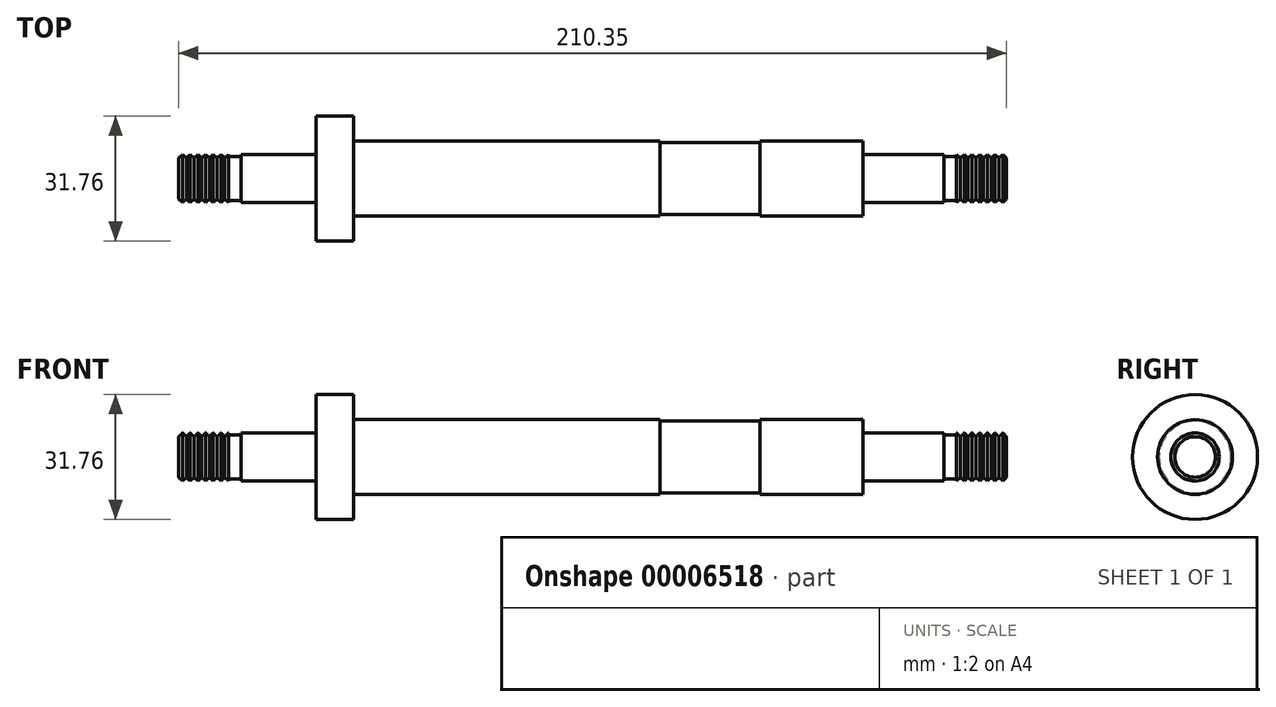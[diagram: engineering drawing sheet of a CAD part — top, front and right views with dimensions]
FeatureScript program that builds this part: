
annotation { "Feature Type Name" : "Feature", "Feature Type Description" : "" }
export const myFeature = defineFeature(function(context is Context, id is Id, definition is map)
    precondition{}
    {
        {
            var Q0;
            Q0=qCreatedBy(makeId("Top.planeOp"),FACE);
            var sketch = newSketch(context, id + "F0", { "sketchPlane" : qUnion([Q0])});
            skLineSegment(sketch, "E0", {"start": v(-288.9, 0) * mm, "end": v(293.4, 0) * mm});
            skLineSegment(sketch, "E1", {"start": v(-256.54, 0) * mm, "end": v(-256.54, 6.14) * mm});
            skLineSegment(sketch, "E2", {"start": v(-256.54, 6.14) * mm, "end": v(-243.84, 6.14) * mm});
            skLineSegment(sketch, "E3", {"start": v(-243.84, 6.14) * mm, "end": v(-243.84, 5.59) * mm});
            skLineSegment(sketch, "E4", {"start": v(-243.84, 5.59) * mm, "end": v(-240.66, 5.59) * mm});
            skLineSegment(sketch, "E5", {"start": v(-240.66, 5.59) * mm, "end": v(-240.66, 6.14) * mm});
            skLineSegment(sketch, "E6", {"start": v(-240.66, 6.14) * mm, "end": v(-221.61, 6.14) * mm});
            skLineSegment(sketch, "E7", {"start": v(-221.61, 6.14) * mm, "end": v(-221.61, 15.88) * mm});
            skLineSegment(sketch, "E8", {"start": v(-221.61, 15.88) * mm, "end": v(-212.09, 15.88) * mm});
            skLineSegment(sketch, "E9", {"start": v(-212.09, 15.88) * mm, "end": v(-212.09, 9.51) * mm});
            skLineSegment(sketch, "E10", {"start": v(-212.09, 9.51) * mm, "end": v(-134.3, 9.51) * mm});
            skLineSegment(sketch, "E11", {"start": v(-134.3, 9.51) * mm, "end": v(-134.3, 9.13) * mm});
            skLineSegment(sketch, "E12", {"start": v(-134.3, 9.13) * mm, "end": v(-108.9, 9.13) * mm});
            skLineSegment(sketch, "E13", {"start": v(-108.9, 9.13) * mm, "end": v(-108.9, 9.51) * mm});
            skLineSegment(sketch, "E14", {"start": v(-108.9, 9.51) * mm, "end": v(-82.7, 9.51) * mm});
            skLineSegment(sketch, "E15", {"start": v(-82.7, 9.51) * mm, "end": v(-82.7, 6.14) * mm});
            skLineSegment(sketch, "E16", {"start": v(-82.7, 6.14) * mm, "end": v(-62.07, 6.14) * mm});
            skLineSegment(sketch, "E17", {"start": v(-62.07, 6.14) * mm, "end": v(-62.07, 5.59) * mm});
            skLineSegment(sketch, "E18", {"start": v(-62.07, 5.59) * mm, "end": v(-58.9, 5.59) * mm});
            skLineSegment(sketch, "E19", {"start": v(-58.9, 5.59) * mm, "end": v(-58.9, 6.14) * mm});
            skLineSegment(sketch, "E20", {"start": v(-58.9, 6.14) * mm, "end": v(-46.2, 6.14) * mm});
            skLineSegment(sketch, "E21", {"start": v(-46.2, 6.14) * mm, "end": v(-46.2, 0) * mm});
            skPoint(sketch, "E22", {"position": v(-256.54, 6.14) * mm});
            skPoint(sketch, "E23.1.0.0", {"position": v(-231.18, 6.14) * mm});
            skPoint(sketch, "E23.2.0.0", {"position": v(-205.78, 6.14) * mm});
            skPoint(sketch, "E24", {"position": v(-256.54, 5.15) * mm});
            skPoint(sketch, "E25", {"position": v(-255.56, 6.14) * mm});
            skLineSegment(sketch, "E26", {"start": v(-256.54, 5.15) * mm, "end": v(-255.56, 6.14) * mm});
            skLineSegment(sketch, "E27", {"start": v(-255.56, 6.14) * mm, "end": v(-254.56, 5.15) * mm});
            skLineSegment(sketch, "E28.1.0.0", {"start": v(-254.58, 5.15) * mm, "end": v(-253.6, 6.14) * mm});
            skLineSegment(sketch, "E28.1.0.1", {"start": v(-253.6, 6.14) * mm, "end": v(-252.6, 5.15) * mm});
            skLineSegment(sketch, "E28.2.0.0", {"start": v(-252.63, 5.15) * mm, "end": v(-251.65, 6.14) * mm});
            skLineSegment(sketch, "E28.2.0.1", {"start": v(-251.65, 6.14) * mm, "end": v(-250.65, 5.15) * mm});
            skLineSegment(sketch, "E28.3.0.0", {"start": v(-250.67, 5.15) * mm, "end": v(-249.7, 6.14) * mm});
            skLineSegment(sketch, "E28.3.0.1", {"start": v(-249.7, 6.14) * mm, "end": v(-248.7, 5.15) * mm});
            skLineSegment(sketch, "E28.4.0.0", {"start": v(-248.72, 5.15) * mm, "end": v(-247.74, 6.14) * mm});
            skLineSegment(sketch, "E28.4.0.1", {"start": v(-247.74, 6.14) * mm, "end": v(-246.74, 5.15) * mm});
            skLineSegment(sketch, "E28.5.0.0", {"start": v(-246.77, 5.15) * mm, "end": v(-245.79, 6.14) * mm});
            skLineSegment(sketch, "E28.5.0.1", {"start": v(-245.79, 6.14) * mm, "end": v(-244.79, 5.15) * mm});
            skLineSegment(sketch, "E28.6.0.0", {"start": v(-244.81, 5.15) * mm, "end": v(-243.84, 6.14) * mm});
            skLineSegment(sketch, "E28.6.0.1", {"start": v(-243.84, 6.14) * mm, "end": v(-242.83, 5.15) * mm});
            skLineSegment(sketch, "E28.direction1", {"start": v(-256.54, 5.15) * mm, "end": v(-254.58, 5.15) * mm, "construction": true});
            skPoint(sketch, "E29", {"position": v(-47.17, 6.14) * mm});
            skPoint(sketch, "E30", {"position": v(-46.2, 5.15) * mm});
            skLineSegment(sketch, "E31", {"start": v(-46.2, 5.15) * mm, "end": v(-47.17, 6.14) * mm});
            skLineSegment(sketch, "E32", {"start": v(-47.17, 6.14) * mm, "end": v(-48.15, 5.15) * mm});
            skLineSegment(sketch, "E33.1.0.0", {"start": v(-48.15, 5.15) * mm, "end": v(-49.12, 6.14) * mm});
            skLineSegment(sketch, "E33.1.0.1", {"start": v(-49.12, 6.14) * mm, "end": v(-50.1, 5.15) * mm});
            skLineSegment(sketch, "E33.2.0.0", {"start": v(-50.1, 5.15) * mm, "end": v(-51.08, 6.14) * mm});
            skLineSegment(sketch, "E33.2.0.1", {"start": v(-51.08, 6.14) * mm, "end": v(-52.05, 5.15) * mm});
            skLineSegment(sketch, "E33.3.0.0", {"start": v(-52.05, 5.15) * mm, "end": v(-53.03, 6.14) * mm});
            skLineSegment(sketch, "E33.3.0.1", {"start": v(-53.03, 6.14) * mm, "end": v(-54, 5.15) * mm});
            skLineSegment(sketch, "E33.4.0.0", {"start": v(-54, 5.15) * mm, "end": v(-54.98, 6.14) * mm});
            skLineSegment(sketch, "E33.4.0.1", {"start": v(-54.98, 6.14) * mm, "end": v(-55.96, 5.15) * mm});
            skLineSegment(sketch, "E33.5.0.0", {"start": v(-55.96, 5.15) * mm, "end": v(-56.94, 6.14) * mm});
            skLineSegment(sketch, "E33.5.0.1", {"start": v(-56.94, 6.14) * mm, "end": v(-57.92, 5.15) * mm});
            skLineSegment(sketch, "E33.6.0.0", {"start": v(-57.92, 5.15) * mm, "end": v(-58.9, 6.14) * mm});
            skLineSegment(sketch, "E33.6.0.1", {"start": v(-58.9, 6.14) * mm, "end": v(-59.87, 5.15) * mm});
            skLineSegment(sketch, "E33.direction1", {"start": v(-46.2, 5.15) * mm, "end": v(-48.15, 5.15) * mm, "construction": true});
            skSolve(sketch);
        }
        {
            var Q0;
            {var subQ6=sQuery(id+"F0.wireOp",EDGE,"E3");Q0=makeQuery(id+"F0.imprint","IMPRINT",FACE,{"disambiguationData":[TD([[makeQuery(id+"F0.imprint","IMPRINT",EDGE,{"derivedFrom":subQ6}),-1.0]])]});}
            var Q1;
            Q1=sQuery(id+"F0.wireOp",EDGE,"E0");
            revolve(context, id + "F1", {"entities" : qUnion([Q0]), "axis" : qUnion([Q1]), "revolveType" : RevolveType.FULL});
        }
    });
